# Revit family: HARMANN - REVIT - MAXEE_EC - pionowy
name_source: partatom
category: Wyposażenie mechaniczne
units: mm (PartAtom-declared; Revit-internal decimal feet)

## family parameters
Klasyfikacja = Brak
Oparty na płaszczyźnie roboczej = Nie
Punkt obliczania pomieszczeń = Nie
Tnij formami wycięć po wczytaniu = Nie
Typ części = Normalny
Współdzielony = Nie
Wymiar okrągłego złącza = Użyj średnicy
Zachowaj orientację opisów = Nie
Zawsze pionowo = Tak

## types (5) — shared parameters
Akcesoria od strony ssawnej (WLOT) = Akcesoria od strony ssawnej
Autor = https://www.archispace.com
Domyślna rzędna = 1219.2 mm  [stored 4 ft]
Długość MR = 154 mm  [stored 0.505249 ft]
Długość SGE = 6.5 mm
Klasa odporności ogniowej Tmax = brak
Lookup Table Name = MAXEE EC
Opis = Kanałowy wentylator - uklad wertykalny
Producent = Harmann Polska Sp. z o.o.
Temperatura pracy T = 60 °C
Wysokość FSD = 57 mm  [stored 0.187008 ft]
Zasilanie Ilość faz = 1
Zasilanie fmax = 10 V
Zasilanie fmin = 1 V
Zasilanie napięcie nominalne Unom = 230 V

## per-type parameters (varying)
- MAXEE 315/5100EC: A=380 mm  [stored 1.24672 ft]; Akc ESD=HARMANN - Akcesoria - ESD : ESD 315; Akc MR=HARMANN - Akcesoria - MR : MR 315; Akc RAF=HARMANN - Akcesoria - RAF : RAF 315; Akc RAS=HARMANN - Akcesoria - RAS : RAS 315; Akc RVK=HARMANN - Akcesoria - RVK : RVK 315; Akc RVS=HARMANN - Akcesoria - RVS : RVS 315; Akc SGE=HARMANN - Akcesoria - SGE : SGE 315; Akc SGE dla ESD=HARMANN - Akcesoria - SGE : SGE 355; B=383 mm  [stored 1.25656 ft]; C=355 mm  [stored 1.1647 ft]; Ciśnienie akustyczne nominalne obudowa Lpa=68 dB(A); D=315 mm  [stored 1.03346 ft]; D2=321 mm  [stored 1.05315 ft]; Długość MAXEE=383 mm  [stored 1.25656 ft]; Długość TRA=336 mm  [stored 1.10236 ft]; F=396 mm  [stored 1.29921 ft]; MAXEE=HARMANN - MAXEE : MAXEE 315/5100EC; Masa=17.20 kg; Moc akustyczna nominalna obudowa Lwa=75 dB(A); N1=2 mm; Numer artykułu=15413600; Obroty nominalne nnom=3010.000 obr./min; Powietrze Przepływ Maksymalny Qmax=5150.0 m³/h; Powietrze ciśnienie statyczne maksymalne dPmax=390.0 Pa; R2=157.5 mm  [stored 0.516732 ft]; Wysokość=116.5 mm  [stored 0.382218 ft]; Wysokość FAL=98 mm  [stored 0.321522 ft]; Zasilanie Moc maksymalna Pmax=900 W; Zasilanie natężenie maksymalne Imax=5 A
- MAXEE 355/7100EC: A=420 mm  [stored 1.37795 ft]; Akc ESD=HARMANN - Akcesoria - ESD : ESD 355; Akc MR=HARMANN - Akcesoria - MR : MR 355; Akc RAF=HARMANN - Akcesoria - RAF : RAF 355; Akc RAS=HARMANN - Akcesoria - RAS : RAS 355; Akc RVK=HARMANN - Akcesoria - RVK : RVK 355; Akc RVS=HARMANN - Akcesoria - RVS : RVS 355; Akc SGE=HARMANN - Akcesoria - SGE : SGE 355; Akc SGE dla ESD=HARMANN - Akcesoria - SGE : SGE 400; B=383 mm  [stored 1.25656 ft]; C=395 mm  [stored 1.29593 ft]; Ciśnienie akustyczne nominalne obudowa Lpa=72; D=355 mm  [stored 1.1647 ft]; D2=361 mm  [stored 1.18438 ft]; Długość MAXEE=383 mm  [stored 1.25656 ft]; Długość TRA=336 mm  [stored 1.10236 ft]; F=396 mm  [stored 1.29921 ft]; MAXEE=HARMANN - MAXEE : MAXEE 355/7100EC; Masa=22.00 kg; Moc akustyczna nominalna obudowa Lwa=79; N1=4 mm; Numer artykułu=15412700; Obroty nominalne nnom=3000.000 obr./min; Powietrze Przepływ Maksymalny Qmax=7155.0 m³/h; Powietrze ciśnienie statyczne maksymalne dPmax=500.0 Pa; R2=177.5 mm  [stored 0.582349 ft]; Wysokość=136 mm; Wysokość FAL=99 mm  [stored 0.324803 ft]; Zasilanie Moc maksymalna Pmax=1648 W; Zasilanie natężenie maksymalne Imax=9 A
- MAXEE 400/8900EC: A=480 mm  [stored 1.5748 ft]; Akc ESD=HARMANN - Akcesoria - ESD : ESD 400; Akc MR=HARMANN - Akcesoria - MR : MR 400; Akc RAF=HARMANN - Akcesoria - RAF : RAF 400; Akc RAS=HARMANN - Akcesoria - RAS : RAS 400; Akc RVK=HARMANN - Akcesoria - RVK : RVK 400; Akc RVS=HARMANN - Akcesoria - RVS : RVS 400; Akc SGE=HARMANN - Akcesoria - SGE : SGE 400; Akc SGE dla ESD=HARMANN - Akcesoria - SGE : SGE 450; B=368 mm  [stored 1.20735 ft]; C=450 mm  [stored 1.47638 ft]; Ciśnienie akustyczne nominalne obudowa Lpa=72; D=400 mm  [stored 1.31234 ft]; D2=406 mm  [stored 1.33202 ft]; Długość MAXEE=368 mm  [stored 1.20735 ft]; Długość TRA=321 mm  [stored 1.05315 ft]; F=396 mm  [stored 1.29921 ft]; MAXEE=HARMANN - MAXEE : MAXEE 400/8900EC; Masa=20.40 kg; Moc akustyczna nominalna obudowa Lwa=79; N1=6 mm; Numer artykułu=15409300; Obroty nominalne nnom=2610.000 obr./min; Powietrze Przepływ Maksymalny Qmax=8900.0 m³/h; Powietrze ciśnienie statyczne maksymalne dPmax=510.0 Pa; R2=200 mm  [stored 0.656168 ft]; Wysokość=158.5 mm  [stored 0.520013 ft]; Wysokość FAL=99 mm  [stored 0.324803 ft]; Zasilanie Moc maksymalna Pmax=1460 W; Zasilanie natężenie maksymalne Imax=10 A
- MAXEE 450/11100EC: A=530 mm  [stored 1.73885 ft]; Akc ESD=HARMANN - Akcesoria - ESD : ESD 450; Akc MR=HARMANN - Akcesoria - MR : MR 450; Akc RAF=HARMANN - Akcesoria - RAF : RAF 450; Akc RAS=HARMANN - Akcesoria - RAS : RAS 450; Akc RVK=HARMANN - Akcesoria - RVK : RVK 450; Akc RVS=HARMANN - Akcesoria - RVS : RVS 450; Akc SGE=HARMANN - Akcesoria - SGE : SGE 450; Akc SGE dla ESD=HARMANN - Akcesoria - SGE : SGE 450; B=368 mm  [stored 1.20735 ft]; C=500 mm  [stored 1.64042 ft]; Ciśnienie akustyczne nominalne obudowa Lpa=66 dB(A); D=450 mm  [stored 1.47638 ft]; D2=456 mm  [stored 1.49606 ft]; Długość MAXEE=368 mm  [stored 1.20735 ft]; Długość TRA=321 mm  [stored 1.05315 ft]; F=396 mm  [stored 1.29921 ft]; MAXEE=HARMANN - MAXEE : MAXEE 450/11100EC; Masa=22.60 kg; Moc akustyczna nominalna obudowa Lwa=73 dB(A); N1=7 mm; Numer artykułu=15626200; Obroty nominalne nnom=23000.000 obr./min; Powietrze Przepływ Maksymalny Qmax=11160.0 m³/h; Powietrze ciśnienie statyczne maksymalne dPmax=360.0 Pa; R2=225 mm  [stored 0.738189 ft]; Wysokość=183.5 mm; Wysokość FAL=99 mm  [stored 0.324803 ft]; Zasilanie Moc maksymalna Pmax=1255 W; Zasilanie natężenie maksymalne Imax=10 A
- MAXEE 500/9800EC: A=590 mm  [stored 1.9357 ft]; Akc ESD=HARMANN - Akcesoria - ESD : ESD 500; Akc MR=HARMANN - Akcesoria - MR : MR 500; Akc RAF=HARMANN - Akcesoria - RAF : RAF 500; Akc RAS=HARMANN - Akcesoria - RAS : RAS 500; Akc RVK=HARMANN - Akcesoria - RVK : RVK 500; Akc RVS=HARMANN - Akcesoria - RVS : RVS 500; Akc SGE=HARMANN - Akcesoria - SGE : SGE 500; Akc SGE dla ESD=HARMANN - Akcesoria - SGE : SGE 500; B=443 mm  [stored 1.45341 ft]; C=560 mm  [stored 1.83727 ft]; Ciśnienie akustyczne nominalne obudowa Lpa=60 dB(A); D=500 mm  [stored 1.64042 ft]; D2=506 mm  [stored 1.6601 ft]; Długość MAXEE=443 mm  [stored 1.45341 ft]; Długość TRA=396 mm  [stored 1.29921 ft]; F=465 mm  [stored 1.52559 ft]; MAXEE=HARMANN - MAXEE : MAXEE 500/9800EC; Masa=32.80 kg; Moc akustyczna nominalna obudowa Lwa=67dB(A); N1=9 mm; Numer artykułu=15411300; Obroty nominalne nnom=1510.000 obr./min; Powietrze Przepływ Maksymalny Qmax=11640.0 m³/h; Powietrze ciśnienie statyczne maksymalne dPmax=260.0 Pa; R2=250 mm  [stored 0.82021 ft]; Wysokość=208.5 mm; Wysokość FAL=99 mm  [stored 0.324803 ft]; Zasilanie Moc maksymalna Pmax=1164 W; Zasilanie natężenie maksymalne Imax=6 A

note: column(s) folded — value = type name in every type: Model

note: [stored X ft] marks values corroborated as IEEE doubles in the binary element streams (Revit-internal decimal feet)

## geometry (parser evidence)
native form markers: Sweep x28
no freeform markers — native parametric forms only
